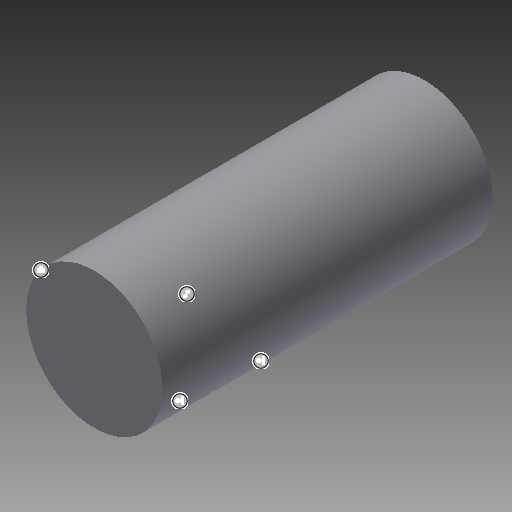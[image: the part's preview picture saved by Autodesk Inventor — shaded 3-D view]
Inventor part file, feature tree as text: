
AUTODESK INVENTOR PART (.ipt)
format: ipt  version: 2017.3 (Build 213256000, 256)  size: 104,448 bytes
history: native  units: mm
features: extrude x1, sketch x1
ambient origin geometry x8: Origin, YZ Plane, XZ Plane, XY Plane, X Axis, Y Axis, Z Axis, Center Point
bodies: Solid1 (feature_tree)
feature tree (2):
  extrude  "Extrusion1"  TaperAngle=0.0deg  [1 undecoded]
  sketch  "Sketch1"  dims[d2=0.0mm d3=0.0mm d4=0.0mm d9=0.0mm d10=0.0mm]
note: 1 required parameter value undecoded (feature->parameter linkage not recoverable at this tier; creation-order binding heuristic only, values carry confidence <= 0.55)
